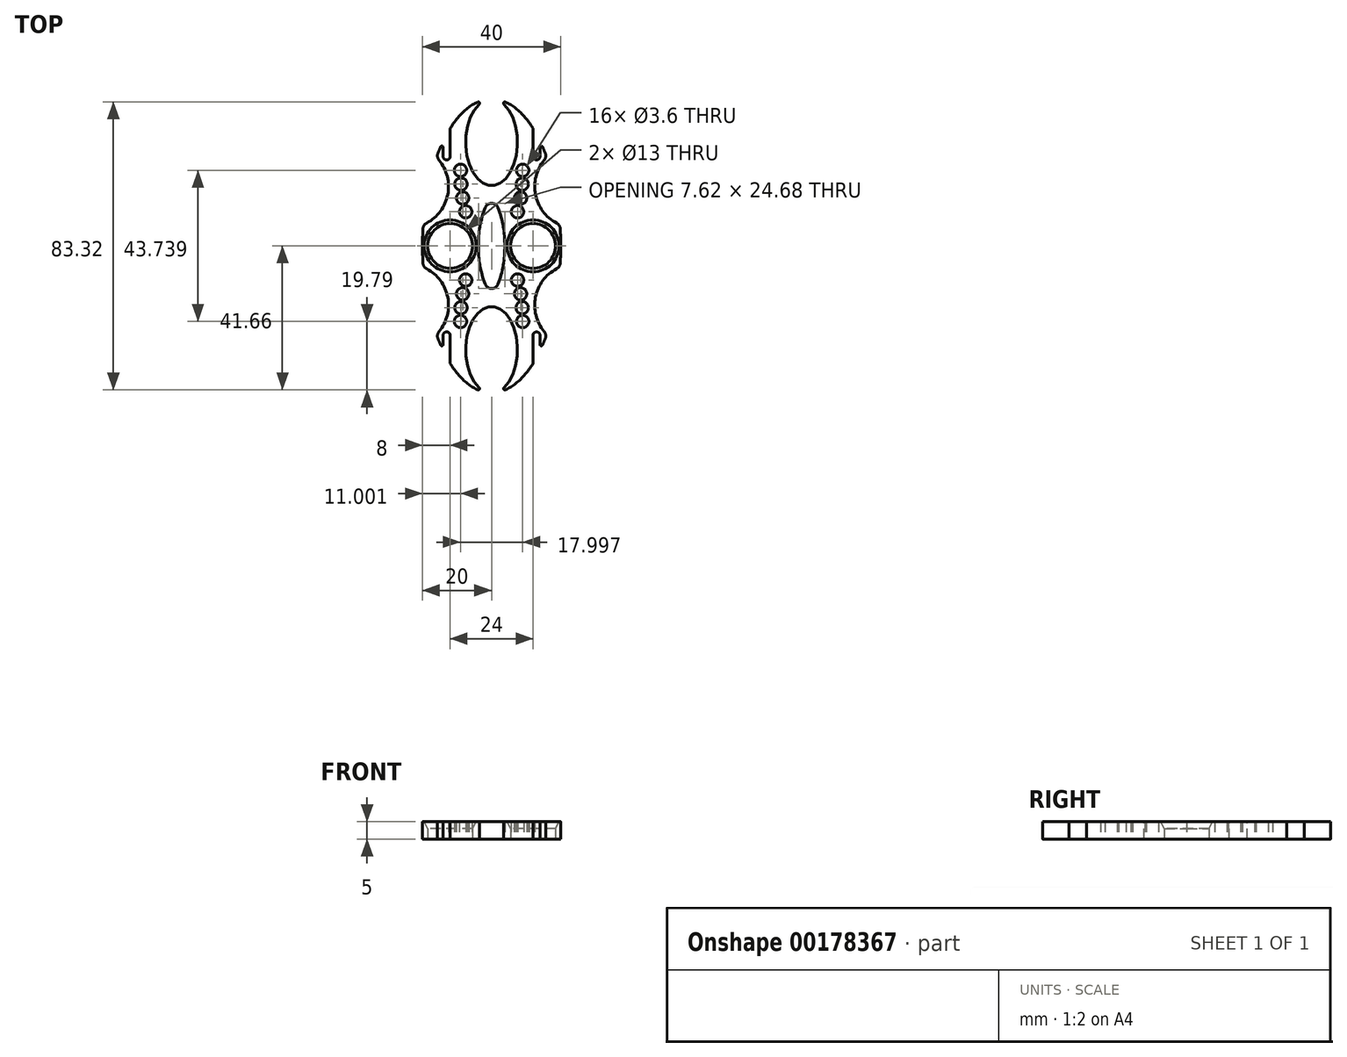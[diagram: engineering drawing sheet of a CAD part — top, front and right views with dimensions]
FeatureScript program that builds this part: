
annotation { "Feature Type Name" : "Feature", "Feature Type Description" : "" }
export const myFeature = defineFeature(function(context is Context, id is Id, definition is map)
    precondition{}
    {
        {
            var Q0;
            Q0=qCreatedBy(makeId("Top.planeOp"),FACE);
            var sketch = newSketch(context, id + "F0", { "sketchPlane" : qUnion([Q0])});
            skPoint(sketch, "E0.middle", {"position": v(0, 0) * mm});
            skArc(sketch, "E1", {"start": v(-18.5, 0) * mm, "mid": v(-12, -6.5) * mm, "end": v(-5.5, 0) * mm});
            skEllipticalArc(sketch, "E2", {});
            skEllipticalArc(sketch, "E3", {});
            skEllipticalArc(sketch, "E4", {"construction": true});
            skCircle(sketch, "E5", {"center": v(-9, -21.87) * mm, "radius": 1.8 * mm});
            skCircle(sketch, "E6", {"center": v(-8.86, -17.87) * mm, "radius": 1.8 * mm});
            skCircle(sketch, "E7", {"center": v(-8.38, -13.87) * mm, "radius": 1.8 * mm});
            skPoint(sketch, "E8.MirrorP", {"position": v(0, -42.5) * mm});
            skPoint(sketch, "E9.MirrorCS.end.orphan", {"position": v(-5.5, 0) * mm});
            skPoint(sketch, "E9.MirrorCS.start.orphan", {"position": v(-18.5, 0) * mm});
            skLineSegment(sketch, "E10", {"start": v(0, -17.5) * mm, "end": v(0, 0) * mm});
            skLineSegment(sketch, "E11", {"start": v(-18.5, 0) * mm, "end": v(-20, 0) * mm});
            skLineSegment(sketch, "E12", {"start": v(0, 0) * mm, "end": v(-5.5, 0) * mm});
            skCircle(sketch, "E13", {"center": v(-7.5, -9.87) * mm, "radius": 1.8 * mm});
            skCircle(sketch, "E14", {"center": v(-13, -25.87) * mm, "radius": 1 * mm});
            skLineSegment(sketch, "E15", {"start": v(-14, -25.87) * mm, "end": v(-14, -30.35) * mm});
            skLineSegment(sketch, "E16", {"start": v(-12, -25.87) * mm, "end": v(-12, -34) * mm});
            skArc(sketch, "E17", {"start": v(-15.96, -25.61) * mm, "mid": v(-12.68, -14.86) * mm, "end": v(-19.79, -6.15) * mm});
            skArc(sketch, "E18", {"start": v(-3.81, 0) * mm, "mid": v(-2.9, -7.79) * mm, "end": v(0, -15.08) * mm});
            const initialGuessF0  = {"E2": [0, 0, 0, -1, 0.0425, 0.02, 4.71238898038469, 0], "E3": [0, -0.03, 0, -1, 0.0125, 0.0075, 3.141592653589793, 0], "E4": [0, -0.0215, 0, -1, 0.021, 0.009, 3.141592653589793, 0]};
            skSetInitialGuess(sketch, initialGuessF0);
            skSolve(sketch);
        }
        {
            var Q0;
            Q0=makeQuery(id+"F0.imprint","IMPRINT",FACE,{"disambiguationData":[TD([[makeQuery(id+"F0.imprint","IMPRINT",EDGE,{"derivedFrom":sQuery(id+"F0.wireOp",EDGE,"bTXWge0H-BZcX-p2Xg-9qWs-Ipd22LkfonOr")}),-1.0]])]});
            var Q1;
            {var subQ3=sQuery(id+"F0.wireOp",EDGE,"E1");Q1=makeQuery(id+"F0.imprint","IMPRINT",FACE,{"disambiguationData":[TD([[makeQuery(id+"F0.imprint","IMPRINT",EDGE,{"derivedFrom":subQ3}),-1.0]])]});}
            extrude(context, id + "F1", {"entities" : qUnion([Q0, Q1]), "depth" : 5 * mm});
        }
        {
            var Q0;
            Q0=makeQuery(id+"F1.opExtrude","SWEPT_EDGE",EDGE,{"disambiguationData":[OSD([sQuery(id+"F0.wireOp",EDGE,"E2"),sQuery(id+"F0.wireOp",EDGE,"E3")])]});
            var Q1;
            Q1=makeQuery(id+"F1.opExtrude","SWEPT_EDGE",EDGE,{"disambiguationData":[OSD([sQuery(id+"F0.wireOp",EDGE,"E2"),sQuery(id+"F0.wireOp",EDGE,"E15")])]});
            fillet(context, id + "F2", {"entities" : qUnion([Q0, Q1]), "radius" : 0.4 * mm, "tangentPropagation" : true, "allowEdgeOverflow" : false});
        }
        {
            var Q0;
            Q0=makeQuery(id+"F1.opExtrude","SWEPT_BODY",BODY,{"disambiguationData":[OSD([sQuery(id+"F0.wireOp",EDGE,"E1"),sQuery(id+"F0.wireOp",EDGE,"E2"),sQuery(id+"F0.wireOp",EDGE,"E3"),sQuery(id+"F0.wireOp",EDGE,"E5"),sQuery(id+"F0.wireOp",EDGE,"E6"),sQuery(id+"F0.wireOp",EDGE,"E7"),sQuery(id+"F0.wireOp",EDGE,"E10"),sQuery(id+"F0.wireOp",EDGE,"E11"),sQuery(id+"F0.wireOp",EDGE,"E12"),sQuery(id+"F0.wireOp",EDGE,"E13"),sQuery(id+"F0.wireOp",EDGE,"E14"),sQuery(id+"F0.wireOp",EDGE,"E15"),sQuery(id+"F0.wireOp",EDGE,"E16")])]});
            var Q1;
            Q1=makeQuery(id+"F1.opExtrude","SWEPT_FACE",FACE,{"disambiguationData":[OSD([sQuery(id+"F0.wireOp",EDGE,"E10")])]});
            mirror(context, id + "F3", {"operationType" : NewBodyOperationType.ADD, "entities" : qUnion([Q0]), "mirrorPlane" : qUnion([Q1])});
        }
        {
            var Q0;
            Q0=makeQuery(id+"F1.opExtrude","SWEPT_BODY",BODY,{"disambiguationData":[OSD([sQuery(id+"F0.wireOp",EDGE,"E1"),sQuery(id+"F0.wireOp",EDGE,"E2"),sQuery(id+"F0.wireOp",EDGE,"E3"),sQuery(id+"F0.wireOp",EDGE,"E5"),sQuery(id+"F0.wireOp",EDGE,"E6"),sQuery(id+"F0.wireOp",EDGE,"E7"),sQuery(id+"F0.wireOp",EDGE,"E10"),sQuery(id+"F0.wireOp",EDGE,"E11"),sQuery(id+"F0.wireOp",EDGE,"E12"),sQuery(id+"F0.wireOp",EDGE,"E13"),sQuery(id+"F0.wireOp",EDGE,"E14"),sQuery(id+"F0.wireOp",EDGE,"E15"),sQuery(id+"F0.wireOp",EDGE,"E16")])]});
            var Q1;
            Q1=makeQuery(id+"F1.opExtrude","SWEPT_FACE",FACE,{"disambiguationData":[OSD([sQuery(id+"F0.wireOp",EDGE,"E12")])]});
            mirror(context, id + "F4", {"operationType" : NewBodyOperationType.ADD, "entities" : qUnion([Q0]), "mirrorPlane" : qUnion([Q1])});
        }
        {
            var Q0;
            {var subQ0=makeQuery(id+"F1.opExtrude","SWEPT_EDGE",EDGE,{"disambiguationData":[OSD([sQuery(id+"F0.wireOp",EDGE,"E10"),sQuery(id+"F0.wireOp",EDGE,"E18")])]});Q0=makeQuery(id+"F4.opPattern","COPY",EDGE,{"derivedFrom":makeQuery(id+"F3.boolean.opBoolean","MERGE",EDGE,{"derivedFrom":[subQ0,makeQuery(id+"F3.opPattern","COPY",EDGE,{"derivedFrom":subQ0,"instanceName":"1"})]}),"instanceName":"1"});}
            var Q1;
            {var subQ0=makeQuery(id+"F1.opExtrude","SWEPT_EDGE",EDGE,{"disambiguationData":[OSD([sQuery(id+"F0.wireOp",EDGE,"E10"),sQuery(id+"F0.wireOp",EDGE,"E18")])]});Q1=makeQuery(id+"F3.boolean.opBoolean","MERGE",EDGE,{"derivedFrom":[subQ0,makeQuery(id+"F3.opPattern","COPY",EDGE,{"derivedFrom":subQ0,"instanceName":"1"})]});}
            var Q2;
            {var subQ0=sQuery(id+"F0.wireOp",EDGE,"E17");var subQ1=sQuery(id+"F0.wireOp",EDGE,"E2");Q2=makeQuery(id+"F3.opPattern","COPY",EDGE,{"derivedFrom":makeQuery(id+"F1.opExtrude","SWEPT_EDGE",EDGE,{"disambiguationData":[OSD([subQ1,subQ0]),TDD([makeQuery(id+"F0.imprint","INTERSECT",VERTEX,{"disambiguationData":[OD(1.0)],"derivedFrom":[subQ1,subQ0]})])]}),"instanceName":"1"});}
            var Q3;
            {var subQ0=sQuery(id+"F0.wireOp",EDGE,"E17");var subQ1=sQuery(id+"F0.wireOp",EDGE,"E2");Q3=makeQuery(id+"F4.opPattern","COPY",EDGE,{"derivedFrom":makeQuery(id+"F3.opPattern","COPY",EDGE,{"derivedFrom":makeQuery(id+"F1.opExtrude","SWEPT_EDGE",EDGE,{"disambiguationData":[OSD([subQ1,subQ0]),TDD([makeQuery(id+"F0.imprint","INTERSECT",VERTEX,{"disambiguationData":[OD(1.0)],"derivedFrom":[subQ1,subQ0]})])]}),"instanceName":"1"}),"instanceName":"1"});}
            var Q4;
            {var subQ0=sQuery(id+"F0.wireOp",EDGE,"E17");var subQ1=sQuery(id+"F0.wireOp",EDGE,"E2");Q4=makeQuery(id+"F1.opExtrude","SWEPT_EDGE",EDGE,{"disambiguationData":[OSD([subQ1,subQ0]),TDD([makeQuery(id+"F0.imprint","INTERSECT",VERTEX,{"disambiguationData":[OD(1.0)],"derivedFrom":[subQ1,subQ0]})])]});}
            var Q5;
            {var subQ0=sQuery(id+"F0.wireOp",EDGE,"E17");var subQ1=sQuery(id+"F0.wireOp",EDGE,"E2");Q5=makeQuery(id+"F4.opPattern","COPY",EDGE,{"derivedFrom":makeQuery(id+"F1.opExtrude","SWEPT_EDGE",EDGE,{"disambiguationData":[OSD([subQ1,subQ0]),TDD([makeQuery(id+"F0.imprint","INTERSECT",VERTEX,{"disambiguationData":[OD(1.0)],"derivedFrom":[subQ1,subQ0]})])]}),"instanceName":"1"});}
            var Q6;
            {var subQ0=sQuery(id+"F0.wireOp",EDGE,"E17");var subQ1=sQuery(id+"F0.wireOp",EDGE,"E2");Q6=makeQuery(id+"F1.opExtrude","SWEPT_EDGE",EDGE,{"disambiguationData":[OSD([subQ1,subQ0]),TDD([makeQuery(id+"F0.imprint","INTERSECT",VERTEX,{"disambiguationData":[OD(0.0)],"derivedFrom":[subQ1,subQ0]})])]});}
            var Q7;
            {var subQ0=sQuery(id+"F0.wireOp",EDGE,"E17");var subQ1=sQuery(id+"F0.wireOp",EDGE,"E2");Q7=makeQuery(id+"F3.opPattern","COPY",EDGE,{"derivedFrom":makeQuery(id+"F1.opExtrude","SWEPT_EDGE",EDGE,{"disambiguationData":[OSD([subQ1,subQ0]),TDD([makeQuery(id+"F0.imprint","INTERSECT",VERTEX,{"disambiguationData":[OD(0.0)],"derivedFrom":[subQ1,subQ0]})])]}),"instanceName":"1"});}
            var Q8;
            {var subQ0=sQuery(id+"F0.wireOp",EDGE,"E17");var subQ1=sQuery(id+"F0.wireOp",EDGE,"E2");Q8=makeQuery(id+"F4.opPattern","COPY",EDGE,{"derivedFrom":makeQuery(id+"F3.opPattern","COPY",EDGE,{"derivedFrom":makeQuery(id+"F1.opExtrude","SWEPT_EDGE",EDGE,{"disambiguationData":[OSD([subQ1,subQ0]),TDD([makeQuery(id+"F0.imprint","INTERSECT",VERTEX,{"disambiguationData":[OD(0.0)],"derivedFrom":[subQ1,subQ0]})])]}),"instanceName":"1"}),"instanceName":"1"});}
            var Q9;
            {var subQ0=sQuery(id+"F0.wireOp",EDGE,"E17");var subQ1=sQuery(id+"F0.wireOp",EDGE,"E2");Q9=makeQuery(id+"F4.opPattern","COPY",EDGE,{"derivedFrom":makeQuery(id+"F1.opExtrude","SWEPT_EDGE",EDGE,{"disambiguationData":[OSD([subQ1,subQ0]),TDD([makeQuery(id+"F0.imprint","INTERSECT",VERTEX,{"disambiguationData":[OD(0.0)],"derivedFrom":[subQ1,subQ0]})])]}),"instanceName":"1"});}
            fillet(context, id + "F5", {"entities" : qUnion([Q0, Q1, Q2, Q3, Q4, Q5, Q6, Q7, Q8, Q9]), "radius" : 2 * mm, "tangentPropagation" : true, "allowEdgeOverflow" : false});
        }
        {
            var Q0;
            {var subQ0=makeQuery(id+"F1.opExtrude","CAP_EDGE",EDGE,{"disambiguationData":[OSD([sQuery(id+"F0.wireOp",EDGE,"E1")])],"isStart":false});Q0=makeQuery(id+"F4.boolean.opBoolean","MERGE",EDGE,{"derivedFrom":[subQ0,makeQuery(id+"F4.opPattern","COPY",EDGE,{"derivedFrom":subQ0,"instanceName":"1"})]});}
            var Q1;
            {var subQ0=makeQuery(id+"F3.opPattern","COPY",EDGE,{"derivedFrom":makeQuery(id+"F1.opExtrude","CAP_EDGE",EDGE,{"disambiguationData":[OSD([sQuery(id+"F0.wireOp",EDGE,"E1")])],"isStart":false}),"instanceName":"1"});Q1=makeQuery(id+"F4.boolean.opBoolean","MERGE",EDGE,{"derivedFrom":[subQ0,makeQuery(id+"F4.opPattern","COPY",EDGE,{"derivedFrom":subQ0,"instanceName":"1"})]});}
            chamfer(context, id + "F6", {"entities" : qUnion([Q0, Q1]), "chamferType" : ChamferType.TWO_OFFSETS, "width1" : 2 * mm, "oppositeDirection" : false, "width2" : 1 * mm, "tangentPropagation" : true});
        }
    });
